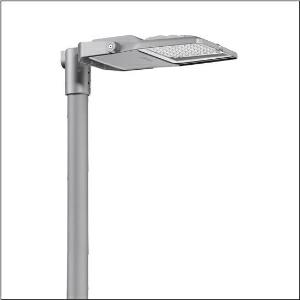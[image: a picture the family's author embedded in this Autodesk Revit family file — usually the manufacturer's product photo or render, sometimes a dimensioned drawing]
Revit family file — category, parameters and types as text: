
# Revit family: floodlight_fl_21_iq_mini___pl52_5xa7771d2d3a_64cb
name_source: partatom
category: Lighting Fixtures
units: mm (PartAtom-declared; Revit-internal decimal feet)

## family parameters
Cut with Voids When Loaded = No
Host = Face
Light Source = No
Part Type = Normal
Room Calculation Point = No
Round Connector Dimension = Use Diameter
Shared = No

## types (1)
- --- (1 x LED, 17830 lm, 143 W, 3000K)
    Apparent Load = 143 VA
    CIE Flux Codes = 26 60 98 100 100
    Color Rendering = 70
    Color Temperature = 3000K
    Default Elevation = 1800 mm
    Description = Floodlight FL 21 iQ mini, floodlight, primary light control with lens, of PMMA, primary optical cover: protective disc, of toughened safety glass, transparent, light distribution: PL52, light emission: direct distribution, installation type: surface-mounted, LED, High Power LED, rated luminous flux: 17.830lm, luminous efficacy: 125lm/W, light colour: 730, colour temperature: 3000K, control: Auto-Match, Temp-Guard, Lumen-Switch, Night-Set, Smart-Wire, Light-Fading, Desk-Remote (wireless, voltage-free reading and setting of iQ features in the workshop via application-optimized NFC function/RFID function), optimised constant luminous flux control (CLO 2.0), with terminal, 6-pole, mains connection: 220..240V, AC, 50/60Hz, start of lifetime: 143W, end of service life: 152W, reduction: 61W, luminaire housing, of diecast aluminium, powder-coated, Siteco® metallic grey (DB 702S), corrosivity category C5 mid according to DIN EN ISO 12944, sealing non-destructively replaceable, please order mast flange separately, mast bracket, of steel, galvanised, powder-coated, Siteco® metallic grey (DB 702S), protection rating (complete): IP66, insulation class (complete): insulation class II (safety insulation), certification: CE, ENEC, VDE, protection symbol: D, impact resistance: IK08, permissible operating ambient temperature: -40..+40°C, permissible operating ambient temperature for outdoor applications: -40..+50°C, standard: DIN EN 12944, LABS conformity tested according to VDMA 24364:2018-05, packaging unit: 1 piece

Light Distribution: PL52
    Height = 70 mm
    Lamp = 1 x LED
    Lamp Light Flux = 17830 lm
    Lamp Power = 143 W
    Lamp count = 1
    Length = 485 mm
    Luminous efficacy = 125 lm/W
    Manufacturer = Siteco
    ModVariant = No
    Model = 5XA7771D2D3A
    Number of Poles = 1
    OnlyDefault = Yes
    Power Factor = 1
    Product Name = Floodlight FL 21 iQ mini | PL52
    Product group = floodlight | pylon annexe
    ProductGroupID = 6200
    Protection Class = Protection class II
    Protection Degree = IP 66
    RLX_Detail_Level = 1
    RLX_Emergency_Light_Flux = 0 lm
    RLX_Emergency_Type = 0
    RLX_Emergency_Type_DB = No
    RlxData = <blob elided: 101601 chars, md5=42e39660>
    Socket = socket
    Standby Power = 0 W
    System Light Flux = 17830 lm
    System Power = 143 W
    Type Comments = factory setting: luminous flux: 100 % | dim-lin: 254 | 730 mA
    Type Image = l_1007125.jpg
    URL = http://relux.com
    VarID = @adj_114129
    Voltage = 0 V
    Weight = 0.00 kg
    Width = 337 mm

## geometry (parser evidence)
native form markers: Blend x4, Sweep x13
no freeform markers — native parametric forms only
